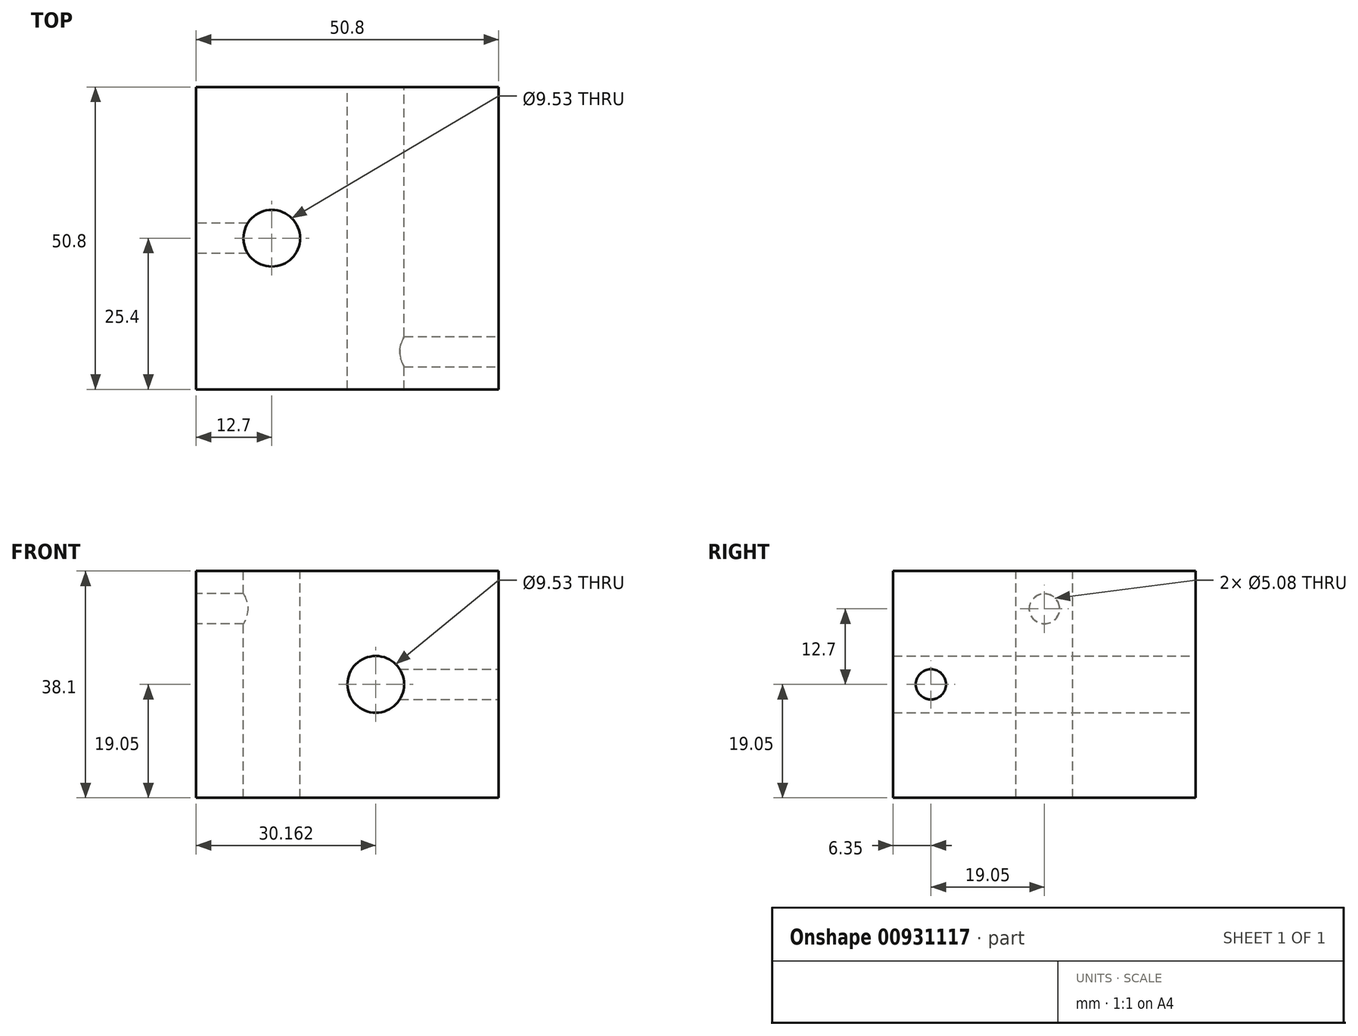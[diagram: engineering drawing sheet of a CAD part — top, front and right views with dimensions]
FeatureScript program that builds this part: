
annotation { "Feature Type Name" : "Feature", "Feature Type Description" : "" }
export const myFeature = defineFeature(function(context is Context, id is Id, definition is map)
    precondition{}
    {
        {
            var Q0;
            Q0=qCreatedBy(makeId("Front.planeOp"),FACE);
            var sketch = newSketch(context, id + "F0", { "sketchPlane" : qUnion([Q0])});
            skLineSegment(sketch, "E0.bottom", {"start": v(25.4, 19.05) * mm, "end": v(-25.4, 19.05) * mm});
            skLineSegment(sketch, "E0.top", {"start": v(25.4, -19.05) * mm, "end": v(-25.4, -19.05) * mm});
            skLineSegment(sketch, "E0.left", {"start": v(25.4, 19.05) * mm, "end": v(25.4, -19.05) * mm});
            skLineSegment(sketch, "E0.right", {"start": v(-25.4, 19.05) * mm, "end": v(-25.4, -19.05) * mm});
            skPoint(sketch, "E0.middle", {"position": v(0, 0) * mm});
            skSolve(sketch);
        }
        {
            var Q0;
            Q0 = qSketchRegion(id + "F0", true);
            extrude(context, id + "F1", {"entities" : qUnion([Q0]), "depth" : 50.8 * mm, "offsetDistance" : 25.4 * mm});
        }
        {
            var Q0;
            Q0=makeQuery(id+"F1.opExtrude","CAP_FACE",FACE,{"disambiguationData":[OSD([sQuery(id+"F0.wireOp",EDGE,"E0.bottom"),sQuery(id+"F0.wireOp",EDGE,"E0.top"),sQuery(id+"F0.wireOp",EDGE,"E0.left"),sQuery(id+"F0.wireOp",EDGE,"E0.right")])],"isStart":true});
            var sketch = newSketch(context, id + "F2", { "sketchPlane" : qUnion([Q0])});
            skCircle(sketch, "E1", {"center": v(-4.76, 0) * mm, "radius": 4.76 * mm});
            skSolve(sketch);
        }
        {
            var Q0;
            Q0 = qSketchRegion(id + "F2", true);
            extrude(context, id + "F3", {"entities" : qUnion([Q0]), "operationType" : NewBodyOperationType.REMOVE, "endBound" : BoundingType.THROUGH_ALL, "oppositeDirection" : true, "depth" : 25.4 * mm, "offsetDistance" : 25.4 * mm});
        }
        {
            var Q0;
            Q0=makeQuery(id+"F1.opExtrude","SWEPT_FACE",FACE,{"disambiguationData":[OSD([sQuery(id+"F0.wireOp",EDGE,"E0.bottom")])]});
            var sketch = newSketch(context, id + "F4", { "sketchPlane" : qUnion([Q0])});
            skCircle(sketch, "E2", {"center": v(-12.7, -25.4) * mm, "radius": 4.76 * mm});
            skSolve(sketch);
        }
        {
            var Q0;
            Q0 = qSketchRegion(id + "F4", true);
            extrude(context, id + "F5", {"entities" : qUnion([Q0]), "operationType" : NewBodyOperationType.REMOVE, "endBound" : BoundingType.THROUGH_ALL, "oppositeDirection" : true, "depth" : 25.4 * mm, "offsetDistance" : 25.4 * mm});
        }
        {
            var Q0;
            Q0=makeQuery(id+"F1.opExtrude","SWEPT_FACE",FACE,{"disambiguationData":[OSD([sQuery(id+"F0.wireOp",EDGE,"E0.right")])]});
            var sketch = newSketch(context, id + "F6", { "sketchPlane" : qUnion([Q0])});
            skCircle(sketch, "E3", {"center": v(25.4, 12.7) * mm, "radius": 2.54 * mm});
            skPoint(sketch, "E3.centerSnap0", {"position": v(25.4, 19.05) * mm});
            skPoint(sketch, "E3.centerSnap1", {"position": v(50.8, 0) * mm});
            skSolve(sketch);
        }
        {
            var Q0;
            Q0 = qSketchRegion(id + "F6", true);
            extrude(context, id + "F7", {"entities" : qUnion([Q0]), "operationType" : NewBodyOperationType.REMOVE, "oppositeDirection" : true, "depth" : 12.7 * mm, "offsetDistance" : 25.4 * mm});
        }
        {
            var Q0;
            Q0=makeQuery(id+"F1.opExtrude","SWEPT_FACE",FACE,{"disambiguationData":[OSD([sQuery(id+"F0.wireOp",EDGE,"E0.left")])]});
            var sketch = newSketch(context, id + "F8", { "sketchPlane" : qUnion([Q0])});
            skCircle(sketch, "E4", {"center": v(-44.45, 0) * mm, "radius": 2.54 * mm});
            skSolve(sketch);
        }
        {
            var Q0;
            Q0 = qSketchRegion(id + "F8", true);
            extrude(context, id + "F9", {"entities" : qUnion([Q0]), "operationType" : NewBodyOperationType.REMOVE, "oppositeDirection" : true, "depth" : 19.05 * mm, "offsetDistance" : 25.4 * mm});
        }
    });
